# Revit family: ACO_PitLok_Plastic
name_source: partatom
category: Electrical Equipment
revit_build: Autodesk Revit 2015 (Build: 20140903_1530(x64)
units: mm (PartAtom-declared; Revit-internal decimal feet)

## types (7) — shared parameters
Description = ACO PITLOK® High Security Trafficable Enclosures
MF Number = 337173
Manufacturer = ACO Pty Ltd
Model = ACO PitLok®
UF Number = G4010.10
URL = http://www.acoaus.com.au

## per-type parameters (varying)
| type | 1000HP15_visibility | 1000HP_visibility | 800P_visibility | Clear Opening Dimensions | Lid part number | P4_visibility | P5_visibiliy | P6_visibility | P8_visibility | Pit Part Number | Plinth Part Number | overall depth | overall weight | type_index |
| 1000HP10 Assembly – ACO PitLok SCEC (SL1) | No | Yes | No | 990 x 990 mm | 142238 | No | No | No | No | -- | 142238 | 200 mm  [stored 0.656168 ft] | 500 kg | 6 |
| P5 Assembly – ACO PitLok SCEC (SL1) | No | No | No | 603 x 353  x 581 mm | 142240 | No | Yes | No | No | 7604299 | 142235 | 785 mm | 220 kg | 2 |
| P6 Assembly – ACO PitLok SCEC (SL1) | No | No | No | 1268 x 455 x 616 mm | 142241 | No | No | Yes | No | 75475 | 142236 | 820 mm  [stored 2.69029 ft] | 390 kg | 3 |
| P8 Assembly – ACO PitLok SCEC (SL1) | No | No | No | 1268 x 455 x 836 mm | 142241 | No | No | No | Yes | 75019 | 142236 | 1040 mm  [stored 3.41207 ft] | 399 kg | 4 |
| 800P Assembly – ACO PitLok SCEC (SL1) | No | No | Yes | 715 x 715 mm | 142367 | No | No | No | No | -- | 142366 | 150 mm  [stored 0.492126 ft] | 390 kg | 5 |
| P4 Assembly – ACO PitLok SCEC (SL1) | No | No | No | 605 x 300 x 745 mm | 142239 | Yes | No | No | No | 75957 | 142234 | 950 mm  [stored 3.1168 ft] | 204 kg | 1 |
| 1000HP15 Assembly – ACO PitLok SCEC (SL1) | Yes | No | No | 990 x 990 mm | 142519 | No | No | No | No | -- | 142519 | 220 mm  [stored 0.721785 ft] | 1090 kg | 7 |

note: [stored X ft] marks values corroborated as IEEE doubles in the binary element streams (Revit-internal decimal feet)

## geometry (parser evidence)
native form markers: Sweep x21
no freeform markers — native parametric forms only
